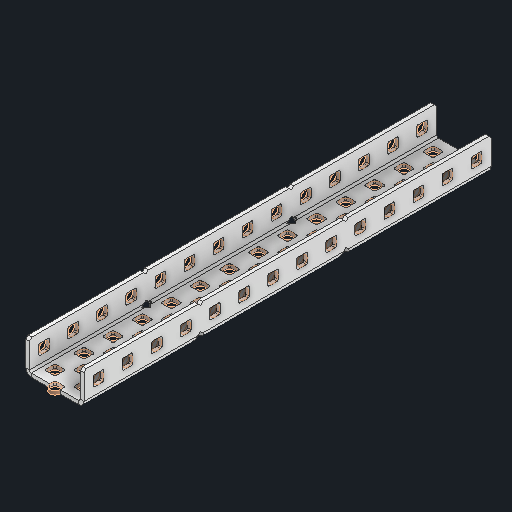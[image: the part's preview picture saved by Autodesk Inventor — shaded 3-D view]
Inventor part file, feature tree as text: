
AUTODESK INVENTOR PART (.ipt)
format: ipt  version: 2024 (Build 280153000, 153)  size: 1,232,896 bytes
history: native  units: in
note: dims shown in document units (in); Inventor stores cm internally (conversion verified against a paired STEP export)
features: other x146, sketch x5, sheet_metal_op x1
ambient origin geometry x8: Origin, YZ Plane, XZ Plane, XY Plane, X Axis, Y Axis, Z Axis, Center Point
bodies: Solid1 (feature_tree)
feature tree (152):
  other  "Alu C 1x2x1x14.ipt"
  other  "Solid1::Alu C 1x2x1x14.ipt"
  other  "TaggingFeature1"
  sketch  "Sketch1"  dims[d0=0.3937in]
  sketch  "Sketch2"  dims[d1=0.0625in]
  sketch  "Sketch3"
  other  "Flange Pattern Sketch"
  sketch  "Sketch9"
  sheet_metal_op  "Body Pattern Sketch"
  other  "Arc Length"
  sketch  "Sketch14"
  other  "Flange Pattern Plane"
  other  "Srf1"
  other  "Srf2"
  other  "Srf3"
  other  "Srf4"
  other  "Srf5"
  other  "Srf6"
  other  "Srf7"
  other  "Srf8"
  other  "Srf9"
  other  "Srf10"
  other  "Srf11"
  other  "Srf12"
  other  "Srf13"
  other  "Srf14"
  other  "Srf15"
  other  "Srf16"
  other  "Srf17"
  other  "Srf18"
  other  "Srf19"
  other  "Srf20"
  other  "Srf21"
  other  "Srf22"
  other  "Srf23"
  other  "Srf24"
  other  "Srf25"
  other  "Srf26"
  other  "Srf27"
  other  "Srf28"
  other  "Srf29"
  other  "Srf30"
  other  "Srf31"
  other  "Srf32"
  other  "Srf33"
  other  "Srf34"
  other  "Srf35"
  other  "Srf36"
  other  "Srf37"
  other  "Srf38"
  other  "Srf39"
  other  "Srf40"
  other  "Srf41"
  other  "Srf42"
  other  "Srf43"
  other  "Srf44"
  other  "Srf45"
  other  "Srf46"
  other  "Srf47"
  other  "Srf48"
  other  "Srf49"
  other  "Srf50"
  other  "Srf51"
  other  "Srf52"
  other  "Srf53"
  other  "Srf54"
  other  "Srf55"
  other  "Srf56"
  other  "Srf57"
  other  "Srf58"
  other  "Srf59"
  other  "Srf60"
  other  "Srf61"
  other  "Srf62"
  other  "Srf63"
  other  "Srf64"
  other  "Srf65"
  other  "Srf66"
  other  "Srf67"
  other  "Srf68"
  other  "Srf69"
  other  "Srf70"
  other  "Srf1::Derived"
  other  "Srf2::Derived"
  other  "Srf823::Derived"
  other  "Srf824::Derived"
  other  "Srf825::Derived"
  other  "Srf826::Derived"
  other  "Srf827::Derived"
  other  "Srf828::Derived"
  other  "Srf829::Derived"
  other  "Srf922::Derived"
  other  "Srf923::Derived"
  other  "Srf924::Derived"
  other  "Srf925::Derived"
  other  "Srf926::Derived"
  other  "Srf1143::Derived"
  other  "Srf1144::Derived"
  other  "Srf1145::Derived"
  other  "Srf1146::Derived"
  other  "Srf1147::Derived"
  other  "Srf1148::Derived"
  other  "Srf1149::Derived"
  other  "Srf1150::Derived"
  other  "Srf1151::Derived"
  other  "Srf1152::Derived"
  other  "Srf1153::Derived"
  other  "Srf1154::Derived"
  other  "Srf1155::Derived"
  other  "Srf1156::Derived"
  other  "Srf91::Derived"
  other  "Srf92::Derived"
  other  "Srf856::Derived"
  other  "Srf857::Derived"
  other  "Srf858::Derived"
  other  "Srf859::Derived"
  other  "Srf860::Derived"
  other  "Srf861::Derived"
  other  "Srf862::Derived"
  other  "Srf959::Derived"
  other  "Srf960::Derived"
  other  "Srf961::Derived"
  other  "Srf962::Derived"
  other  "Srf963::Derived"
  other  "Srf1199::Derived"
  other  "Srf1200::Derived"
  other  "Srf1201::Derived"
  other  "Srf1202::Derived"
  other  "Srf1203::Derived"
  other  "Srf1204::Derived"
  other  "Srf1205::Derived"
  other  "Srf1206::Derived"
  other  "Srf1207::Derived"
  other  "Srf1208::Derived"
  other  "Srf1209::Derived"
  other  "Srf1210::Derived"
  other  "Srf1211::Derived"
  other  "Srf1212::Derived"
  other  "Srf786::Derived"
  other  "Srf889::Derived"
  other  "Srf890::Derived"
  other  "Srf891::Derived"
  other  "Srf892::Derived"
  other  "Srf893::Derived"
  other  "Srf894::Derived"
  other  "Srf895::Derived"
  other  "Srf896::Derived"
  other  "Srf996::Derived"
  other  "Srf997::Derived"
  other  "Srf998::Derived"
  other  "Srf999::Derived"
  other  "Srf1000::Derived"
